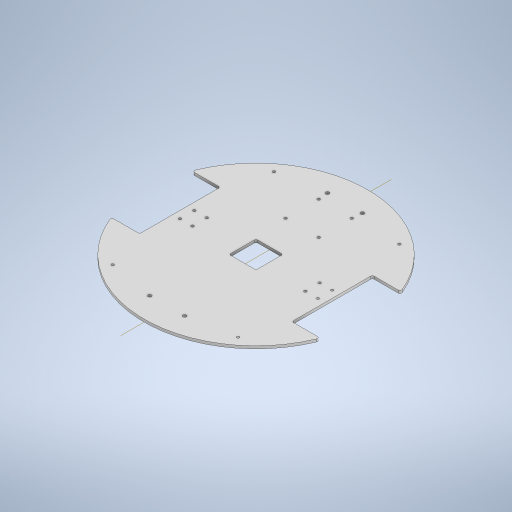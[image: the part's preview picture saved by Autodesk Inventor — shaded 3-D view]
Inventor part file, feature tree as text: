
AUTODESK INVENTOR PART (.ipt)
format: ipt  version: 2023.3 (Build 273359000, 359)  size: 281,088 bytes
history: native  units: mm
features: extrude x1, sketch x1
ambient origin geometry x8: Origin, YZ Plane, XZ Plane, XY Plane, X Axis, Y Axis, Z Axis, Center Point
bodies: Body1 (feature_tree)
feature tree (2):
  extrude  "Extrusion2"  Depth=3.0mm
  sketch  "Sketch1"  dims[d0=250.0mm d2=85.0mm d29=3.0mm d30=0.0mm]
